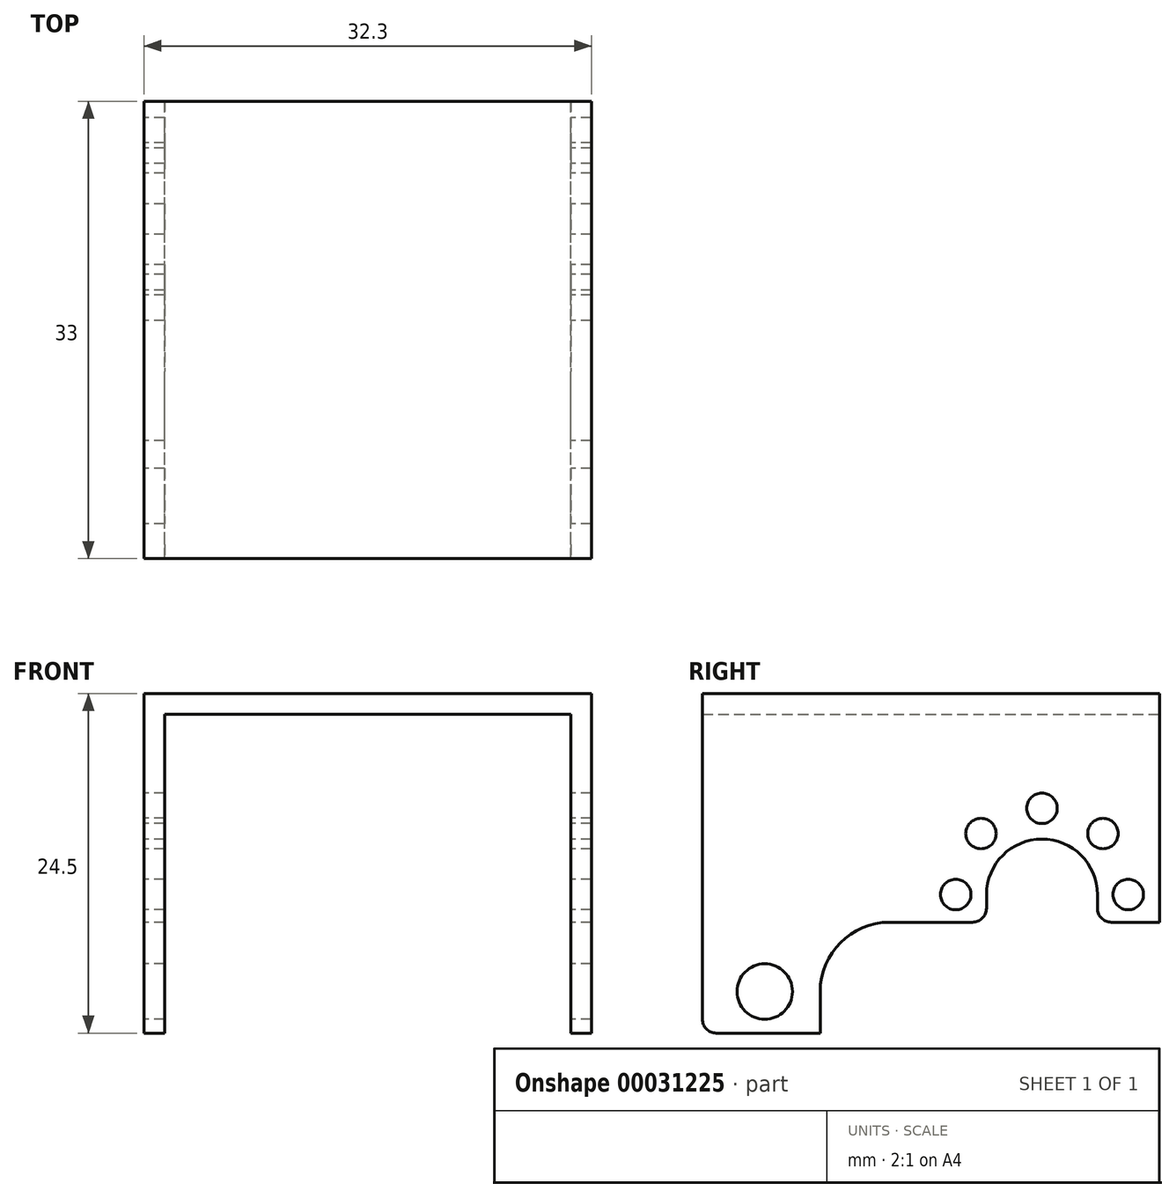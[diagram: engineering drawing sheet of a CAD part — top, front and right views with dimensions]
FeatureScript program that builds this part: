
annotation { "Feature Type Name" : "Feature", "Feature Type Description" : "" }
export const myFeature = defineFeature(function(context is Context, id is Id, definition is map)
    precondition{}
    {
        {
            var Q0;
            Q0=qCreatedBy(makeId("Front.planeOp"),FACE);
            var sketch = newSketch(context, id + "F0", { "sketchPlane" : qUnion([Q0])});
            skLineSegment(sketch, "E0.bottom", {"start": v(0, 0) * mm, "end": v(1.5, 0) * mm});
            skLineSegment(sketch, "E0.top", {"start": v(0, 24.5) * mm, "end": v(32.3, 24.5) * mm});
            skLineSegment(sketch, "E0.left", {"start": v(0, 0) * mm, "end": v(0, 24.5) * mm});
            skLineSegment(sketch, "E0.right", {"start": v(32.3, 0) * mm, "end": v(32.3, 24.5) * mm});
            skLineSegment(sketch, "E1.top", {"start": v(1.5, 23) * mm, "end": v(30.8, 23) * mm});
            skLineSegment(sketch, "E1.left", {"start": v(1.5, 0) * mm, "end": v(1.5, 23) * mm});
            skLineSegment(sketch, "E1.right", {"start": v(30.8, 0) * mm, "end": v(30.8, 23) * mm});
            skLineSegment(sketch, "E2.trimOffspring", {"start": v(30.8, 0) * mm, "end": v(32.3, 0) * mm});
            skSolve(sketch);
        }
        {
            var Q0;
            Q0 = qSketchRegion(id + "F0", true);
            extrude(context, id + "F1", {"entities" : qUnion([Q0]), "depth" : 33 * mm});
        }
        {
            var Q0;
            Q0=makeQuery(id+"F1.opExtrude","SWEPT_FACE",FACE,{"disambiguationData":[OSD([sQuery(id+"F0.wireOp",EDGE,"E0.left")])]});
            var sketch = newSketch(context, id + "F2", { "sketchPlane" : qUnion([Q0])});
            skLineSegment(sketch, "E3.bottom", {"start": v(0, 0) * mm, "end": v(24.5, 0) * mm});
            skLineSegment(sketch, "E3.top", {"start": v(0, 8) * mm, "end": v(4.5, 8) * mm});
            skLineSegment(sketch, "E3.left", {"start": v(0, 0) * mm, "end": v(0, 8) * mm});
            skLineSegment(sketch, "E3.right", {"start": v(24.5, 0) * mm, "end": v(24.5, 8) * mm});
            skArc(sketch, "E4", {"start": v(12.5, 10) * mm, "mid": v(8.5, 14) * mm, "end": v(4.5, 10) * mm});
            skCircle(sketch, "E5", {"center": v(14.72, 10) * mm, "radius": 1.1 * mm});
            skCircle(sketch, "E6.1.0", {"center": v(12.9, 14.4) * mm, "radius": 1.1 * mm});
            skCircle(sketch, "E6.2.0", {"center": v(8.5, 16.22) * mm, "radius": 1.1 * mm});
            skCircle(sketch, "E6.3.0", {"center": v(4.1, 14.4) * mm, "radius": 1.1 * mm});
            skCircle(sketch, "E6.4.0", {"center": v(2.28, 10) * mm, "radius": 1.1 * mm});
            skLineSegment(sketch, "E7", {"start": v(4.5, 10) * mm, "end": v(4.5, 8) * mm});
            skLineSegment(sketch, "E8", {"start": v(12.5, 10) * mm, "end": v(12.5, 8) * mm});
            skLineSegment(sketch, "E9.trimOffspring", {"start": v(12.5, 8) * mm, "end": v(24.5, 8) * mm});
            skCircle(sketch, "E10", {"center": v(28.5, 3) * mm, "radius": 2 * mm});
            skSolve(sketch);
        }
        {
            var Q0;
            Q0 = qSketchRegion(id + "F2", true);
            extrude(context, id + "F3", {"entities" : qUnion([Q0]), "operationType" : NewBodyOperationType.REMOVE, "endBound" : BoundingType.THROUGH_ALL, "oppositeDirection" : true, "depth" : 25 * mm});
        }
        {
            var Q0;
            Q0=makeQuery(id+"FhSWsQVfl24fQ8d_1.boolean.opBoolean","COPY",EDGE,{"disambiguationData":[OD(1.0)],"derivedFrom":makeQuery(id+"FhSWsQVfl24fQ8d_1.opExtrude","CAP_EDGE",EDGE,{"disambiguationData":[OSD([sQuery(id+"Fpe3hB4YBDp0oAt_1.wireOp",EDGE,"4bd2b07d-e855-4691-9f5c-57cf29639554.bottom")])],"isStart":false})});
            var Q1;
            Q1=makeQuery(id+"FhSWsQVfl24fQ8d_1.boolean.opBoolean","COPY",EDGE,{"disambiguationData":[OD(0.0)],"derivedFrom":makeQuery(id+"FhSWsQVfl24fQ8d_1.opExtrude","CAP_EDGE",EDGE,{"disambiguationData":[OSD([sQuery(id+"Fpe3hB4YBDp0oAt_1.wireOp",EDGE,"4bd2b07d-e855-4691-9f5c-57cf29639554.bottom")])],"isStart":false})});
            var Q2;
            Q2=makeQuery(id+"F3.boolean.opBoolean","COPY",EDGE,{"disambiguationData":[OD(0.0)],"derivedFrom":makeQuery(id+"F3.opExtrude","SWEPT_EDGE",EDGE,{"disambiguationData":[OSD([sQuery(id+"F2.wireOp",EDGE,"E3.top"),sQuery(id+"F2.wireOp",EDGE,"E7")])]})});
            var Q3;
            Q3=makeQuery(id+"F3.boolean.opBoolean","COPY",EDGE,{"disambiguationData":[OD(0.0)],"derivedFrom":makeQuery(id+"F3.opExtrude","SWEPT_EDGE",EDGE,{"disambiguationData":[OSD([sQuery(id+"F2.wireOp",EDGE,"E8"),sQuery(id+"F2.wireOp",EDGE,"E9.trimOffspring")])]})});
            var Q4;
            Q4=makeQuery(id+"F3.boolean.opBoolean","COPY",EDGE,{"disambiguationData":[OD(0.0)],"derivedFrom":makeQuery(id+"F3.opExtrude","SWEPT_EDGE",EDGE,{"disambiguationData":[OSD([sQuery(id+"F0.wireOp",EDGE,"E0.left"),sQuery(id+"F2.wireOp",EDGE,"E3.top"),sQuery(id+"F2.wireOp",EDGE,"E3.left")])]})});
            var Q5;
            Q5=makeQuery(id+"F3.boolean.opBoolean","COPY",EDGE,{"disambiguationData":[OD(0.0)],"derivedFrom":makeQuery(id+"F3.opExtrude","SWEPT_EDGE",EDGE,{"disambiguationData":[OSD([sQuery(id+"F0.wireOp",EDGE,"E0.bottom"),sQuery(id+"F0.wireOp",EDGE,"E0.left"),sQuery(id+"F2.wireOp",EDGE,"E3.bottom"),sQuery(id+"F2.wireOp",EDGE,"E3.right")])]})});
            var Q6;
            Q6=makeQuery(id+"F1.opExtrude","CAP_EDGE",EDGE,{"disambiguationData":[OSD([sQuery(id+"F0.wireOp",EDGE,"E0.bottom")])],"isStart":false});
            var Q7;
            Q7=makeQuery(id+"F1.opExtrude","CAP_EDGE",EDGE,{"disambiguationData":[OSD([sQuery(id+"F0.wireOp",EDGE,"E2.trimOffspring")])],"isStart":false});
            var Q8;
            Q8=makeQuery(id+"F3.boolean.opBoolean","COPY",EDGE,{"disambiguationData":[OD(1.0)],"derivedFrom":makeQuery(id+"F3.opExtrude","SWEPT_EDGE",EDGE,{"disambiguationData":[OSD([sQuery(id+"F0.wireOp",EDGE,"E0.bottom"),sQuery(id+"F0.wireOp",EDGE,"E0.left"),sQuery(id+"F2.wireOp",EDGE,"E3.bottom"),sQuery(id+"F2.wireOp",EDGE,"E3.right")])]})});
            var Q9;
            Q9=makeQuery(id+"F3.boolean.opBoolean","COPY",EDGE,{"disambiguationData":[OD(1.0)],"derivedFrom":makeQuery(id+"F3.opExtrude","SWEPT_EDGE",EDGE,{"disambiguationData":[OSD([sQuery(id+"F2.wireOp",EDGE,"E8"),sQuery(id+"F2.wireOp",EDGE,"E9.trimOffspring")])]})});
            var Q10;
            Q10=makeQuery(id+"F3.boolean.opBoolean","COPY",EDGE,{"disambiguationData":[OD(1.0)],"derivedFrom":makeQuery(id+"F3.opExtrude","SWEPT_EDGE",EDGE,{"disambiguationData":[OSD([sQuery(id+"F2.wireOp",EDGE,"E3.top"),sQuery(id+"F2.wireOp",EDGE,"E7")])]})});
            var Q11;
            Q11=makeQuery(id+"F3.boolean.opBoolean","COPY",EDGE,{"disambiguationData":[OD(1.0)],"derivedFrom":makeQuery(id+"F3.opExtrude","SWEPT_EDGE",EDGE,{"disambiguationData":[OSD([sQuery(id+"F0.wireOp",EDGE,"E0.left"),sQuery(id+"F2.wireOp",EDGE,"E3.top"),sQuery(id+"F2.wireOp",EDGE,"E3.left")])]})});
            fillet(context, id + "F4", {"entities" : qUnion([Q0, Q1, Q2, Q3, Q4, Q5, Q6, Q7, Q8, Q9, Q10, Q11]), "radius" : 1 * mm, "tangentPropagation" : true, "allowEdgeOverflow" : false});
        }
        {
            var Q0;
            Q0=makeQuery(id+"F3.boolean.opBoolean","COPY",EDGE,{"disambiguationData":[OD(1.0)],"derivedFrom":makeQuery(id+"F3.opExtrude","SWEPT_EDGE",EDGE,{"disambiguationData":[OSD([sQuery(id+"F2.wireOp",EDGE,"E3.right"),sQuery(id+"F2.wireOp",EDGE,"E9.trimOffspring")])]})});
            var Q1;
            Q1=makeQuery(id+"F3.boolean.opBoolean","COPY",EDGE,{"disambiguationData":[OD(0.0)],"derivedFrom":makeQuery(id+"F3.opExtrude","SWEPT_EDGE",EDGE,{"disambiguationData":[OSD([sQuery(id+"F2.wireOp",EDGE,"E3.right"),sQuery(id+"F2.wireOp",EDGE,"E9.trimOffspring")])]})});
            fillet(context, id + "F5", {"entities" : qUnion([Q0, Q1]), "radius" : 5 * mm, "tangentPropagation" : true, "allowEdgeOverflow" : false});
        }
    });
